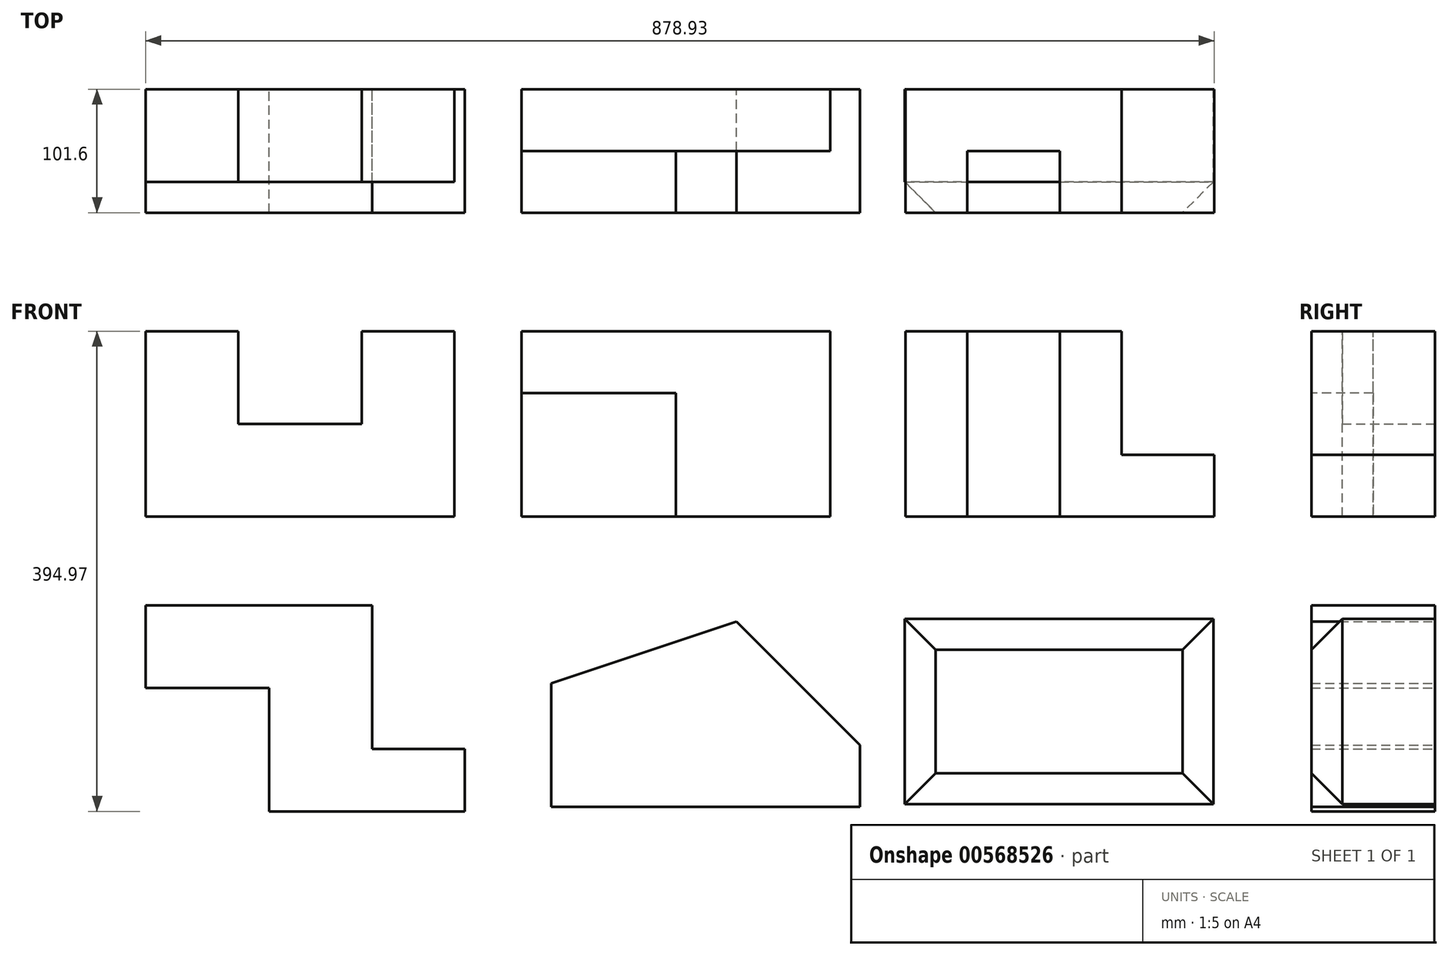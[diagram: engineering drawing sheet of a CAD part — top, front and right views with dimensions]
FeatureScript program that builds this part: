
annotation { "Feature Type Name" : "Feature", "Feature Type Description" : "" }
export const myFeature = defineFeature(function(context is Context, id is Id, definition is map)
    precondition{}
    {
        {
            var Q0;
            Q0=qCreatedBy(makeId("Front.planeOp"),FACE);
            var sketch = newSketch(context, id + "F0", { "sketchPlane" : qUnion([Q0])});
            skLineSegment(sketch, "E0", {"start": v(0, 0) * mm, "end": v(254, 0) * mm});
            skLineSegment(sketch, "E1", {"start": v(254, 0) * mm, "end": v(254, 152.4) * mm});
            skLineSegment(sketch, "E2", {"start": v(254, 152.4) * mm, "end": v(177.8, 152.4) * mm});
            skLineSegment(sketch, "E3", {"start": v(177.8, 152.4) * mm, "end": v(177.8, 76.2) * mm});
            skLineSegment(sketch, "E4", {"start": v(0, 0) * mm, "end": v(0, 152.4) * mm});
            skLineSegment(sketch, "E5", {"start": v(0, 152.4) * mm, "end": v(76.2, 152.4) * mm});
            skLineSegment(sketch, "E6", {"start": v(76.2, 152.4) * mm, "end": v(76.2, 76.2) * mm});
            skLineSegment(sketch, "E7", {"start": v(76.2, 76.2) * mm, "end": v(177.8, 76.2) * mm});
            skSolve(sketch);
        }
        {
            var Q0;
            Q0=makeQuery(id+"F0.imprint","IMPRINT",FACE,{"disambiguationData":[TD([[makeQuery(id+"F0.imprint","IMPRINT",EDGE,{"derivedFrom":sQuery(id+"F0.wireOp",EDGE,"E0")}),1.0]])]});
            extrude(context, id + "F1", {"entities" : qUnion([Q0]), "depth" : 76.2 * mm, "offsetDistance" : 25.4 * mm});
        }
        {
            var Q0;
            Q0=qCreatedBy(makeId("Front.planeOp"),FACE);
            var sketch = newSketch(context, id + "F2", { "sketchPlane" : qUnion([Q0])});
            skLineSegment(sketch, "E8.bottom", {"start": v(309.28, 0) * mm, "end": v(563.28, 0) * mm});
            skLineSegment(sketch, "E8.top", {"start": v(309.28, 152.4) * mm, "end": v(563.28, 152.4) * mm});
            skLineSegment(sketch, "E8.left", {"start": v(309.28, 0) * mm, "end": v(309.28, 152.4) * mm});
            skLineSegment(sketch, "E8.right", {"start": v(563.28, 0) * mm, "end": v(563.28, 152.4) * mm});
            skSolve(sketch);
        }
        {
            var Q0;
            Q0=makeQuery(id+"F2.imprint","IMPRINT",FACE,{"disambiguationData":[TD([[makeQuery(id+"F2.imprint","IMPRINT",EDGE,{"derivedFrom":sQuery(id+"F2.wireOp",EDGE,"E8.bottom")}),1.0]])]});
            extrude(context, id + "F3", {"entities" : qUnion([Q0]), "depth" : 101.6 * mm, "offsetDistance" : 25.4 * mm});
        }
        {
            var Q0;
            Q0=makeQuery(id+"F3.opExtrude","CAP_FACE",FACE,{"disambiguationData":[OSD([sQuery(id+"F2.wireOp",EDGE,"E8.bottom"),sQuery(id+"F2.wireOp",EDGE,"E8.top"),sQuery(id+"F2.wireOp",EDGE,"E8.left"),sQuery(id+"F2.wireOp",EDGE,"E8.right")])],"isStart":false});
            var sketch = newSketch(context, id + "F4", { "sketchPlane" : qUnion([Q0])});
            skLineSegment(sketch, "E9", {"start": v(309.28, 0) * mm, "end": v(309.28, 101.6) * mm});
            skLineSegment(sketch, "E10", {"start": v(309.28, 101.6) * mm, "end": v(436.28, 101.6) * mm});
            skLineSegment(sketch, "E11", {"start": v(436.28, 101.6) * mm, "end": v(436.28, 0) * mm});
            skSolve(sketch);
        }
        {
            var Q0;
            {var subQ2=sQuery(id+"F4.wireOp",EDGE,"E10");Q0=makeQuery(id+"F4.imprint","IMPRINT",FACE,{"disambiguationData":[TD([[makeQuery(id+"F4.imprint","IMPRINT",EDGE,{"derivedFrom":subQ2}),1.0]])]});}
            extrude(context, id + "F5", {"entities" : qUnion([Q0]), "operationType" : NewBodyOperationType.REMOVE, "oppositeDirection" : true, "depth" : 50.8 * mm, "offsetDistance" : 25.4 * mm});
        }
        {
            var Q0;
            Q0=qCreatedBy(makeId("Front.planeOp"),FACE);
            var sketch = newSketch(context, id + "F6", { "sketchPlane" : qUnion([Q0])});
            skLineSegment(sketch, "E12", {"start": v(624.93, 0) * mm, "end": v(624.93, 152.4) * mm});
            skLineSegment(sketch, "E13", {"start": v(624.93, 152.4) * mm, "end": v(675.73, 152.4) * mm});
            skLineSegment(sketch, "E14", {"start": v(624.93, 0) * mm, "end": v(878.93, 0) * mm});
            skLineSegment(sketch, "E15", {"start": v(878.93, 0) * mm, "end": v(878.93, 50.8) * mm});
            skLineSegment(sketch, "E16", {"start": v(878.93, 50.8) * mm, "end": v(802.73, 50.8) * mm});
            skLineSegment(sketch, "E17", {"start": v(802.73, 50.8) * mm, "end": v(802.73, 152.4) * mm});
            skLineSegment(sketch, "E18", {"start": v(802.73, 152.4) * mm, "end": v(751.93, 152.4) * mm});
            skPoint(sketch, "E18.endSnap0", {"position": v(751.93, 0) * mm});
            skLineSegment(sketch, "E19", {"start": v(751.93, 152.4) * mm, "end": v(751.93, 50.8) * mm});
            skLineSegment(sketch, "E20", {"start": v(751.93, 50.8) * mm, "end": v(675.73, 50.8) * mm});
            skLineSegment(sketch, "E21", {"start": v(675.73, 50.8) * mm, "end": v(675.73, 152.4) * mm});
            skLineSegment(sketch, "E22", {"start": v(675.73, 152.4) * mm, "end": v(751.93, 152.4) * mm});
            skSolve(sketch);
        }
        {
            var Q0;
            Q0 = qSketchRegion(id + "F6", true);
            extrude(context, id + "F7", {"entities" : qUnion([Q0]), "depth" : 101.6 * mm, "offsetDistance" : 25.4 * mm});
        }
        {
            var Q0;
            Q0=makeQuery(id+"F7.opExtrude","CAP_FACE",FACE,{"disambiguationData":[OSD([sQuery(id+"F6.wireOp",EDGE,"E12"),sQuery(id+"F6.wireOp",EDGE,"E13"),sQuery(id+"F6.wireOp",EDGE,"E14"),sQuery(id+"F6.wireOp",EDGE,"E15"),sQuery(id+"F6.wireOp",EDGE,"E16"),sQuery(id+"F6.wireOp",EDGE,"E17"),sQuery(id+"F6.wireOp",EDGE,"E18"),sQuery(id+"F6.wireOp",EDGE,"E22")])],"isStart":false});
            var sketch = newSketch(context, id + "F8", { "sketchPlane" : qUnion([Q0])});
            skLineSegment(sketch, "E23", {"start": v(675.73, 152.4) * mm, "end": v(675.73, 0) * mm});
            skLineSegment(sketch, "E24", {"start": v(751.93, 152.4) * mm, "end": v(751.93, 0) * mm});
            skSolve(sketch);
        }
        {
            var Q0;
            Q0 = qSketchRegion(id + "F8", true);
            var Q1;
            {var subQ0=sQuery(id+"F8.wireOp",EDGE,"E23");Q1=makeQuery(id+"F8.imprint","IMPRINT",FACE,{"disambiguationData":[TD([[makeQuery(id+"F8.imprint","IMPRINT",EDGE,{"derivedFrom":subQ0}),1.0]])]});}
            extrude(context, id + "F9", {"entities" : qUnion([Q0, Q1]), "operationType" : NewBodyOperationType.REMOVE, "oppositeDirection" : true, "depth" : 50.8 * mm, "offsetDistance" : 25.4 * mm});
        }
        {
            var Q0;
            Q0=qCreatedBy(makeId("Front.planeOp"),FACE);
            var sketch = newSketch(context, id + "F10", { "sketchPlane" : qUnion([Q0])});
            skLineSegment(sketch, "E25", {"start": v(0, -73.23) * mm, "end": v(0, -140.97) * mm});
            skLineSegment(sketch, "E26", {"start": v(0, -140.97) * mm, "end": v(101.6, -140.97) * mm});
            skLineSegment(sketch, "E27", {"start": v(101.6, -140.97) * mm, "end": v(101.6, -242.57) * mm});
            skLineSegment(sketch, "E28", {"start": v(101.6, -242.57) * mm, "end": v(262.47, -242.57) * mm});
            skLineSegment(sketch, "E29", {"start": v(262.47, -242.57) * mm, "end": v(262.47, -191.23) * mm});
            skLineSegment(sketch, "E30", {"start": v(262.47, -191.23) * mm, "end": v(186.27, -191.23) * mm});
            skLineSegment(sketch, "E31", {"start": v(186.27, -191.23) * mm, "end": v(186.27, -73.23) * mm});
            skLineSegment(sketch, "E32", {"start": v(186.27, -73.23) * mm, "end": v(0, -73.23) * mm});
            skSolve(sketch);
        }
        {
            var Q0;
            Q0=makeQuery(id+"F10.imprint","IMPRINT",FACE,{"disambiguationData":[TD([[makeQuery(id+"F10.imprint","IMPRINT",EDGE,{"derivedFrom":sQuery(id+"F10.wireOp",EDGE,"E25")}),1.0]])]});
            extrude(context, id + "F11", {"entities" : qUnion([Q0]), "depth" : 101.6 * mm, "offsetDistance" : 25.4 * mm});
        }
        {
            var Q0;
            Q0=qCreatedBy(makeId("Front.planeOp"),FACE);
            var sketch = newSketch(context, id + "F12", { "sketchPlane" : qUnion([Q0])});
            skLineSegment(sketch, "E33", {"start": v(333.73, -238.92) * mm, "end": v(587.73, -238.92) * mm});
            skLineSegment(sketch, "E34", {"start": v(333.73, -238.92) * mm, "end": v(333.73, -137.32) * mm});
            skLineSegment(sketch, "E35", {"start": v(587.73, -238.92) * mm, "end": v(587.73, -188.12) * mm});
            skLineSegment(sketch, "E36", {"start": v(486.13, -86.52) * mm, "end": v(333.73, -137.32) * mm});
            skLineSegment(sketch, "E37", {"start": v(486.13, -86.52) * mm, "end": v(587.73, -188.12) * mm});
            skSolve(sketch);
        }
        {
            var Q0;
            Q0=makeQuery(id+"F12.imprint","IMPRINT",FACE,{"disambiguationData":[TD([[makeQuery(id+"F12.imprint","IMPRINT",EDGE,{"derivedFrom":sQuery(id+"F12.wireOp",EDGE,"E33")}),1.0]])]});
            extrude(context, id + "F13", {"entities" : qUnion([Q0]), "depth" : 101.6 * mm, "offsetDistance" : 25.4 * mm});
        }
        {
            var Q0;
            Q0=qCreatedBy(makeId("Front.planeOp"),FACE);
            var sketch = newSketch(context, id + "F14", { "sketchPlane" : qUnion([Q0])});
            skLineSegment(sketch, "E38.bottom", {"start": v(624.45, -236.67) * mm, "end": v(878.45, -236.67) * mm});
            skLineSegment(sketch, "E38.top", {"start": v(624.45, -84.27) * mm, "end": v(878.45, -84.27) * mm});
            skLineSegment(sketch, "E38.left", {"start": v(624.45, -236.67) * mm, "end": v(624.45, -84.27) * mm});
            skLineSegment(sketch, "E38.right", {"start": v(878.45, -236.67) * mm, "end": v(878.45, -84.27) * mm});
            skSolve(sketch);
        }
        {
            var Q0;
            Q0=makeQuery(id+"F14.imprint","IMPRINT",FACE,{"disambiguationData":[TD([[makeQuery(id+"F14.imprint","IMPRINT",EDGE,{"derivedFrom":sQuery(id+"F14.wireOp",EDGE,"E38.bottom")}),1.0]])]});
            extrude(context, id + "F15", {"entities" : qUnion([Q0]), "depth" : 101.6 * mm, "offsetDistance" : 25.4 * mm});
        }
        {
            var Q0;
            Q0=makeQuery(id+"F15.opExtrude","CAP_FACE",FACE,{"disambiguationData":[OSD([sQuery(id+"F14.wireOp",EDGE,"E38.bottom"),sQuery(id+"F14.wireOp",EDGE,"E38.top"),sQuery(id+"F14.wireOp",EDGE,"E38.left"),sQuery(id+"F14.wireOp",EDGE,"E38.right")])],"isStart":false});
            chamfer(context, id + "F16", {"entities" : qUnion([Q0]), "width" : 25.4 * mm, "tangentPropagation" : true});
        }
    });
